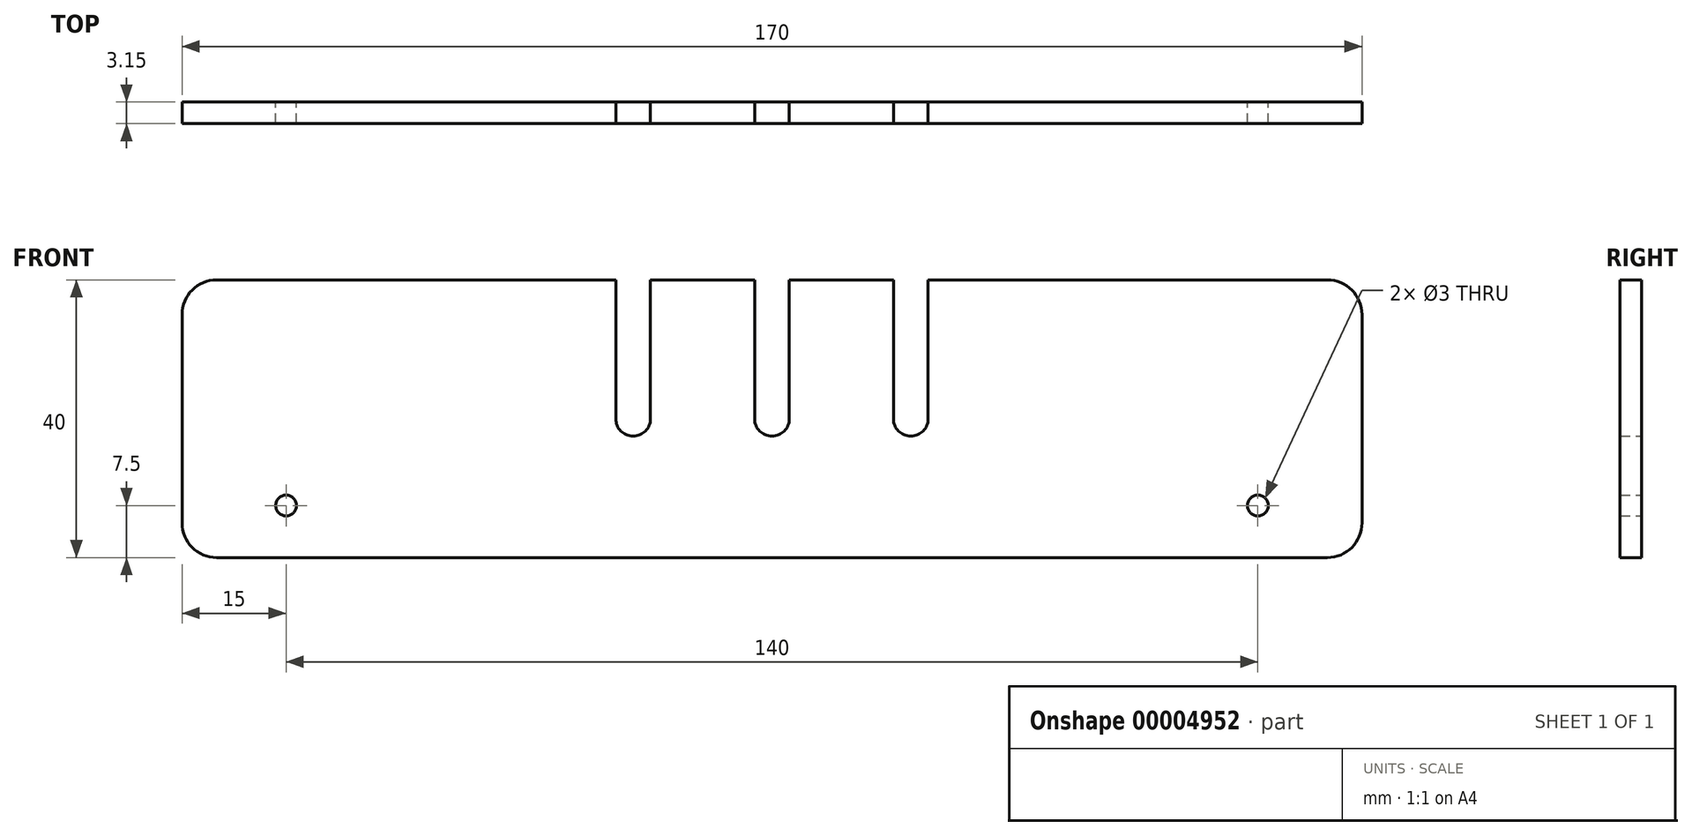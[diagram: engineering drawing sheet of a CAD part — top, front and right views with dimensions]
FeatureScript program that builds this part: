
annotation { "Feature Type Name" : "Feature", "Feature Type Description" : "" }
export const myFeature = defineFeature(function(context is Context, id is Id, definition is map)
    precondition{}
    {
        {
            var Q0;
            Q0=qCreatedBy(makeId("Front.planeOp"),FACE);
            var sketch = newSketch(context, id + "F0", { "sketchPlane" : qUnion([Q0])});
            skLineSegment(sketch, "E0.rect.bottom", {"start": v(85, 20) * mm, "end": v(-85, 20) * mm});
            skLineSegment(sketch, "E0.rect.top", {"start": v(85, -20) * mm, "end": v(-85, -20) * mm});
            skLineSegment(sketch, "E0.rect.left", {"start": v(85, 20) * mm, "end": v(85, -20) * mm});
            skLineSegment(sketch, "E0.rect.right", {"start": v(-85, 20) * mm, "end": v(-85, -20) * mm});
            skPoint(sketch, "E0.rect.middle", {"position": v(0, 0) * mm});
            skLineSegment(sketch, "E1", {"start": v(0, 20) * mm, "end": v(0, -20) * mm, "construction": true});
            skLineSegment(sketch, "E2", {"start": v(-30, 20) * mm, "end": v(-30, -20) * mm, "construction": true});
            skLineSegment(sketch, "E3", {"start": v(-30, 0) * mm, "end": v(0, 0) * mm, "construction": true});
            skCircle(sketch, "E4", {"center": v(0, 0) * mm, "radius": 2.5 * mm});
            skCircle(sketch, "E5", {"center": v(-20, 0) * mm, "radius": 2.5 * mm});
            skCircle(sketch, "E6.MirrorC", {"center": v(20, 0) * mm, "radius": 2.5 * mm});
            skLineSegment(sketch, "E7", {"start": v(-85, -12.5) * mm, "end": v(85, -12.5) * mm, "construction": true});
            skCircle(sketch, "E8", {"center": v(-70, -12.5) * mm, "radius": 1.5 * mm});
            skCircle(sketch, "E9.MirrorC", {"center": v(70, -12.5) * mm, "radius": 1.5 * mm});
            skSolve(sketch);
        }
        {
            var Q0;
            Q0 = qSketchRegion(id + "F0", true);
            extrude(context, id + "F1", {"entities" : qUnion([Q0]), "depth" : 3.15 * mm});
        }
        {
            var Q0;
            Q0=makeQuery(id+"F1.opExtrude","CAP_FACE",FACE,{"disambiguationData":[OSD([sQuery(id+"F0.wireOp",EDGE,"E0.rect.bottom"),sQuery(id+"F0.wireOp",EDGE,"E0.rect.top"),sQuery(id+"F0.wireOp",EDGE,"E0.rect.left"),sQuery(id+"F0.wireOp",EDGE,"E0.rect.right"),sQuery(id+"F0.wireOp",EDGE,"E4"),sQuery(id+"F0.wireOp",EDGE,"E5"),sQuery(id+"F0.wireOp",EDGE,"E6.MirrorC"),sQuery(id+"F0.wireOp",EDGE,"E8"),sQuery(id+"F0.wireOp",EDGE,"E9.MirrorC")])],"isStart":false});
            var sketch = newSketch(context, id + "F2", { "sketchPlane" : qUnion([Q0])});
            skLineSegment(sketch, "E10", {"start": v(0, 0) * mm, "end": v(0, 20) * mm, "construction": true});
            skLineSegment(sketch, "E11.bottom", {"start": v(-22.5, 0) * mm, "end": v(-17.5, 0) * mm});
            skLineSegment(sketch, "E11.top", {"start": v(-22.5, 20) * mm, "end": v(-17.5, 20) * mm});
            skLineSegment(sketch, "E11.left", {"start": v(-22.5, 0) * mm, "end": v(-22.5, 20) * mm});
            skLineSegment(sketch, "E11.right", {"start": v(-17.5, 0) * mm, "end": v(-17.5, 20) * mm});
            skLineSegment(sketch, "E12.MirrorCS", {"start": v(22.5, 0) * mm, "end": v(17.5, 0) * mm});
            skLineSegment(sketch, "E13.MirrorCS", {"start": v(22.5, 20) * mm, "end": v(17.5, 20) * mm});
            skLineSegment(sketch, "E14.MirrorCS", {"start": v(22.5, 0) * mm, "end": v(22.5, 20) * mm});
            skLineSegment(sketch, "E15.MirrorCS", {"start": v(17.5, 0) * mm, "end": v(17.5, 20) * mm});
            skLineSegment(sketch, "E16.bottom", {"start": v(-2.5, 0) * mm, "end": v(2.5, 0) * mm});
            skLineSegment(sketch, "E16.top", {"start": v(-2.5, 20) * mm, "end": v(2.5, 20) * mm});
            skLineSegment(sketch, "E16.left", {"start": v(-2.5, 0) * mm, "end": v(-2.5, 20) * mm});
            skLineSegment(sketch, "E16.right", {"start": v(2.5, 0) * mm, "end": v(2.5, 20) * mm});
            skSolve(sketch);
        }
        {
            var Q0;
            Q0 = qSketchRegion(id + "F2", true);
            extrude(context, id + "F3", {"entities" : qUnion([Q0]), "operationType" : NewBodyOperationType.REMOVE, "oppositeDirection" : true, "depth" : 25 * mm});
        }
        {
            var Q0;
            Q0=makeQuery(id+"F1.opExtrude","SWEPT_EDGE",EDGE,{"disambiguationData":[OSD([sQuery(id+"F0.wireOp",EDGE,"E0.rect.bottom"),sQuery(id+"F0.wireOp",EDGE,"E0.rect.right")])]});
            var Q1;
            Q1=makeQuery(id+"F1.opExtrude","SWEPT_EDGE",EDGE,{"disambiguationData":[OSD([sQuery(id+"F0.wireOp",EDGE,"E0.rect.top"),sQuery(id+"F0.wireOp",EDGE,"E0.rect.right")])]});
            var Q2;
            Q2=makeQuery(id+"F1.opExtrude","SWEPT_EDGE",EDGE,{"disambiguationData":[OSD([sQuery(id+"F0.wireOp",EDGE,"E0.rect.bottom"),sQuery(id+"F0.wireOp",EDGE,"E0.rect.left")])]});
            var Q3;
            Q3=makeQuery(id+"F1.opExtrude","SWEPT_EDGE",EDGE,{"disambiguationData":[OSD([sQuery(id+"F0.wireOp",EDGE,"E0.rect.top"),sQuery(id+"F0.wireOp",EDGE,"E0.rect.left")])]});
            var Q4;
            Q4=makeQuery(id+"F3.boolean.opBoolean","COPY",EDGE,{"derivedFrom":makeQuery(id+"F3.opExtrude","SWEPT_EDGE",EDGE,{"disambiguationData":[OSD([sQuery(id+"F0.wireOp",EDGE,"E0.rect.bottom"),sQuery(id+"F2.wireOp",EDGE,"E11.top"),sQuery(id+"F2.wireOp",EDGE,"E11.left")])]})});
            var Q5;
            Q5=makeQuery(id+"F3.boolean.opBoolean","COPY",EDGE,{"derivedFrom":makeQuery(id+"F3.opExtrude","SWEPT_EDGE",EDGE,{"disambiguationData":[OSD([sQuery(id+"F0.wireOp",EDGE,"E0.rect.bottom"),sQuery(id+"F2.wireOp",EDGE,"E11.top"),sQuery(id+"F2.wireOp",EDGE,"E11.right")])]})});
            var Q6;
            Q6=makeQuery(id+"F3.boolean.opBoolean","COPY",EDGE,{"derivedFrom":makeQuery(id+"F3.opExtrude","SWEPT_EDGE",EDGE,{"disambiguationData":[OSD([sQuery(id+"F0.wireOp",EDGE,"E0.rect.bottom"),sQuery(id+"F2.wireOp",EDGE,"E13.MirrorCS"),sQuery(id+"F2.wireOp",EDGE,"E15.MirrorCS")])]})});
            var Q7;
            Q7=makeQuery(id+"F3.boolean.opBoolean","COPY",EDGE,{"derivedFrom":makeQuery(id+"F3.opExtrude","SWEPT_EDGE",EDGE,{"disambiguationData":[OSD([sQuery(id+"F0.wireOp",EDGE,"E0.rect.bottom"),sQuery(id+"F2.wireOp",EDGE,"E13.MirrorCS"),sQuery(id+"F2.wireOp",EDGE,"E14.MirrorCS")])]})});
            var Q8;
            Q8=makeQuery(id+"F3.boolean.opBoolean","COPY",EDGE,{"derivedFrom":makeQuery(id+"F3.opExtrude","SWEPT_EDGE",EDGE,{"disambiguationData":[OSD([sQuery(id+"F0.wireOp",EDGE,"E0.rect.bottom"),sQuery(id+"F2.wireOp",EDGE,"E16.top"),sQuery(id+"F2.wireOp",EDGE,"E16.left")])]})});
            var Q9;
            Q9=makeQuery(id+"F3.boolean.opBoolean","COPY",EDGE,{"derivedFrom":makeQuery(id+"F3.opExtrude","SWEPT_EDGE",EDGE,{"disambiguationData":[OSD([sQuery(id+"F0.wireOp",EDGE,"E0.rect.bottom"),sQuery(id+"F2.wireOp",EDGE,"E16.top"),sQuery(id+"F2.wireOp",EDGE,"E16.right")])]})});
            fillet(context, id + "F4", {"entities" : qUnion([Q0, Q1, Q2, Q3, Q4, Q5, Q6, Q7, Q8, Q9]), "radius" : 5 * mm, "tangentPropagation" : true, "allowEdgeOverflow" : false});
        }
    });
